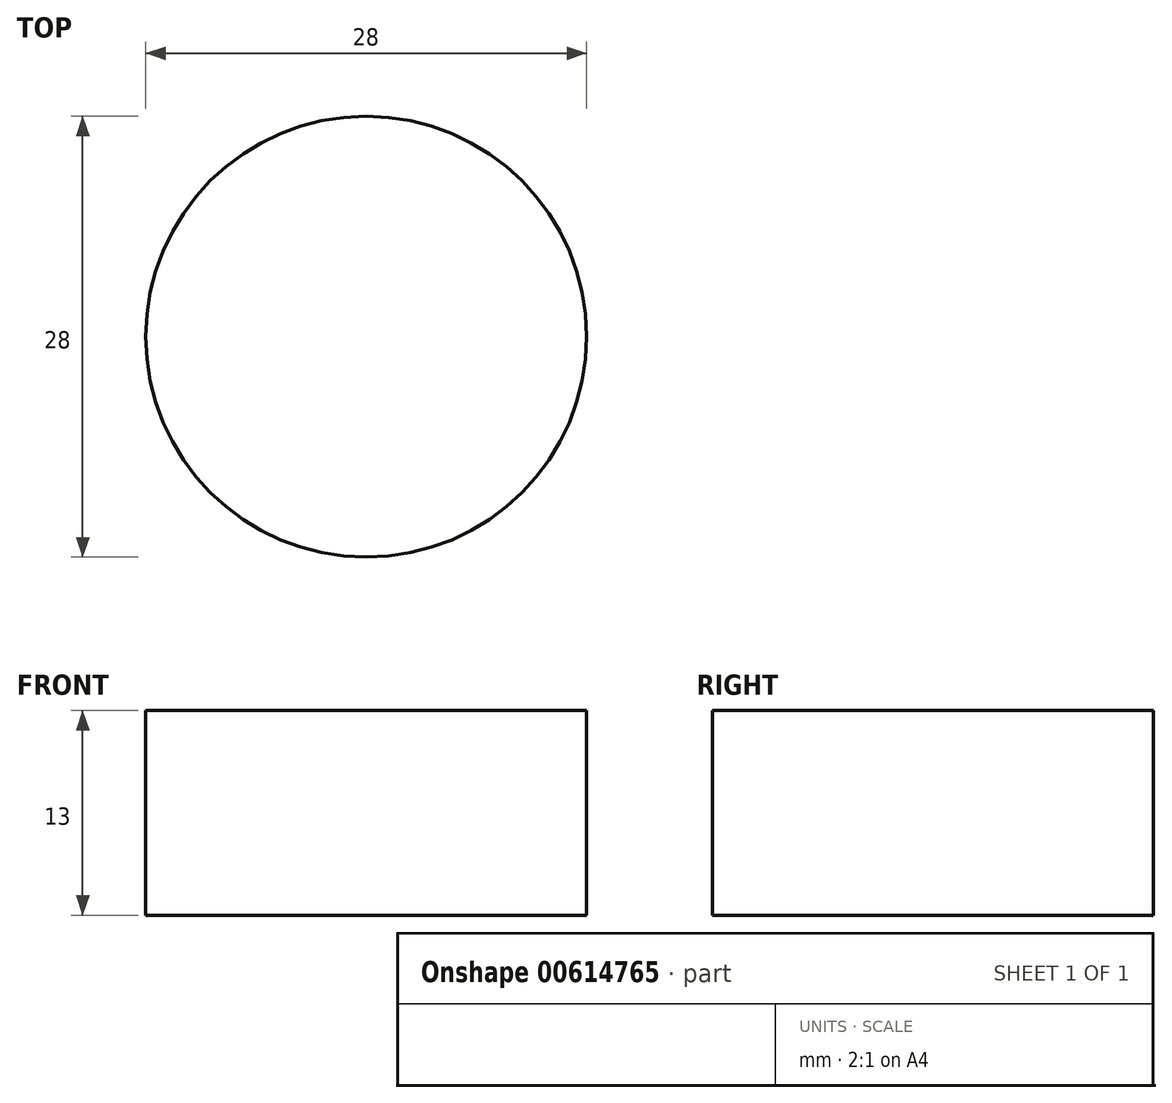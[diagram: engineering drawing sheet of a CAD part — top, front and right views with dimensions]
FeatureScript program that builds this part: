
annotation { "Feature Type Name" : "Feature", "Feature Type Description" : "" }
export const myFeature = defineFeature(function(context is Context, id is Id, definition is map)
    precondition{}
    {
        {
            var Q0;
            Q0=qCreatedBy(makeId("Top.planeOp"),FACE);
            var sketch = newSketch(context, id + "F0", { "sketchPlane" : qUnion([Q0])});
            skCircle(sketch, "E0", {"center": v(0, 0) * mm, "radius": 14 * mm});
            skSolve(sketch);
        }
        {
            var Q0;
            Q0=makeQuery(id+"F0.imprint","IMPRINT",FACE,{"disambiguationData":[TD([[makeQuery(id+"F0.imprint","IMPRINT",EDGE,{"derivedFrom":sQuery(id+"F0.wireOp",EDGE,"E0")}),1.0]])]});
            extrude(context, id + "F1", {"entities" : qUnion([Q0]), "depth" : 13 * mm, "offsetDistance" : 25 * mm});
        }
    });
